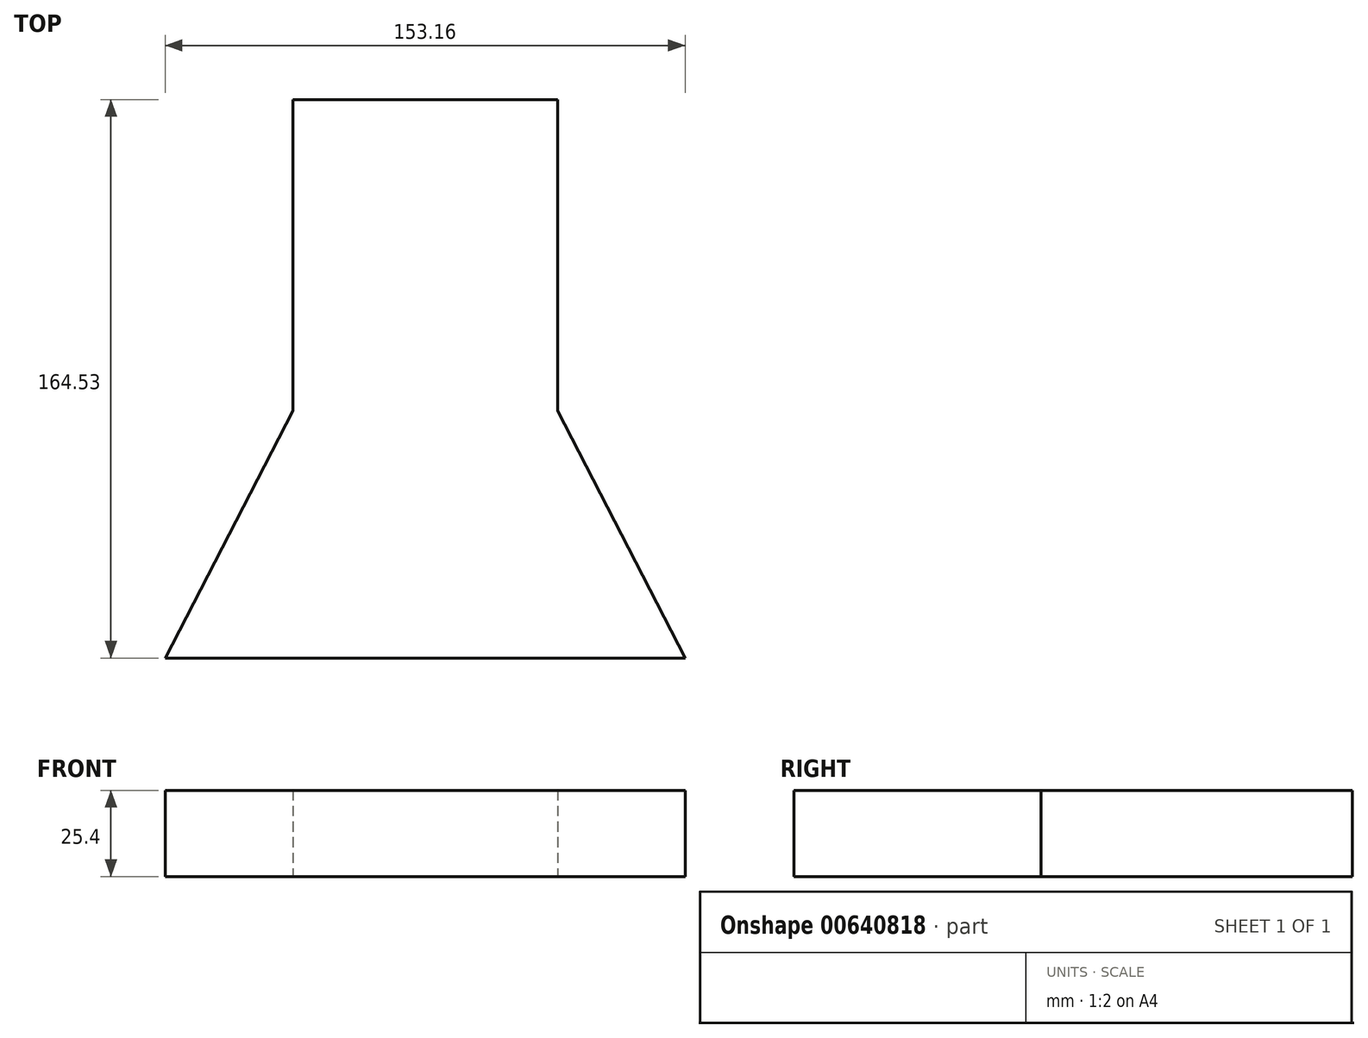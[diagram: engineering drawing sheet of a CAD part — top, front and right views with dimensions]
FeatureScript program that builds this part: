
annotation { "Feature Type Name" : "Feature", "Feature Type Description" : "" }
export const myFeature = defineFeature(function(context is Context, id is Id, definition is map)
    precondition{}
    {
        {
            var Q0;
            Q0=qCreatedBy(makeId("Top.planeOp"),FACE);
            var sketch = newSketch(context, id + "F0", { "sketchPlane" : qUnion([Q0])});
            skLineSegment(sketch, "E0.bottom", {"start": v(76.58, 95.18) * mm, "end": v(-76.58, 95.18) * mm});
            skLineSegment(sketch, "E0.top", {"start": v(76.58, -95.18) * mm, "end": v(-76.58, -95.18) * mm});
            skLineSegment(sketch, "E0.left", {"start": v(76.58, 95.18) * mm, "end": v(76.58, -95.18) * mm});
            skLineSegment(sketch, "E0.right", {"start": v(-76.58, 95.18) * mm, "end": v(-76.58, -95.18) * mm});
            skPoint(sketch, "E0.middle", {"position": v(0, 0) * mm});
            skLineSegment(sketch, "E1.bottom", {"start": v(38.98, 69.35) * mm, "end": v(-38.98, 69.35) * mm});
            skLineSegment(sketch, "E2", {"start": v(-38.98, -22.39) * mm, "end": v(38.98, -22.39) * mm});
            skLineSegment(sketch, "E3", {"start": v(-38.98, -22.39) * mm, "end": v(-38.98, 69.35) * mm});
            skLineSegment(sketch, "E4", {"start": v(38.98, 69.35) * mm, "end": v(38.98, -22.39) * mm});
            skLineSegment(sketch, "E5", {"start": v(38.98, 69.35) * mm, "end": v(76.58, 95.18) * mm});
            skLineSegment(sketch, "E6", {"start": v(-38.98, 69.35) * mm, "end": v(-76.58, 95.18) * mm});
            skLineSegment(sketch, "E7", {"start": v(38.98, -22.39) * mm, "end": v(76.58, -95.18) * mm});
            skLineSegment(sketch, "E8", {"start": v(-38.98, -22.39) * mm, "end": v(-76.58, -95.18) * mm});
            skLineSegment(sketch, "E9", {"start": v(57.78, 8.75) * mm, "end": v(38.98, -22.39) * mm});
            skLineSegment(sketch, "E10", {"start": v(38.98, 69.35) * mm, "end": v(57.78, 48.9) * mm});
            skLineSegment(sketch, "E11", {"start": v(57.78, 48.9) * mm, "end": v(76.58, 95.18) * mm});
            skLineSegment(sketch, "E12", {"start": v(57.78, 8.75) * mm, "end": v(76.58, -95.18) * mm});
            skLineSegment(sketch, "E13", {"start": v(57.78, 48.9) * mm, "end": v(57.78, 8.75) * mm});
            skLineSegment(sketch, "E14.MirrorCS", {"start": v(-57.78, 8.75) * mm, "end": v(-38.98, -22.39) * mm});
            skLineSegment(sketch, "E15.MirrorCS", {"start": v(-57.78, 48.9) * mm, "end": v(-57.78, 8.75) * mm});
            skLineSegment(sketch, "E16.MirrorCS", {"start": v(-38.98, 69.35) * mm, "end": v(-57.78, 48.9) * mm});
            skLineSegment(sketch, "E17.MirrorCS", {"start": v(-57.78, 48.9) * mm, "end": v(-76.58, 95.18) * mm});
            skLineSegment(sketch, "E18.MirrorCS", {"start": v(-57.78, 8.75) * mm, "end": v(-76.58, -95.18) * mm});
            skSolve(sketch);
        }
        {
            var Q0;
            Q0=makeQuery(id+"F0.imprint","IMPRINT",FACE,{"disambiguationData":[TD([[makeQuery(id+"F0.imprint","IMPRINT",EDGE,{"derivedFrom":sQuery(id+"F0.wireOp",EDGE,"E1.bottom")}),1.0]])]});
            extrude(context, id + "F1", {"entities" : qUnion([Q0]), "depth" : 25.4 * mm, "offsetDistance" : 25.4 * mm});
        }
        {
            var Q0;
            Q0=makeQuery(id+"F0.imprint","IMPRINT",FACE,{"disambiguationData":[TD([[makeQuery(id+"F0.imprint","IMPRINT",EDGE,{"derivedFrom":sQuery(id+"F0.wireOp",EDGE,"E0.top")}),-1.0]])]});
            extrude(context, id + "F2", {"entities" : qUnion([Q0]), "operationType" : NewBodyOperationType.ADD, "depth" : 25.4 * mm, "offsetDistance" : 25.4 * mm});
        }
    });
